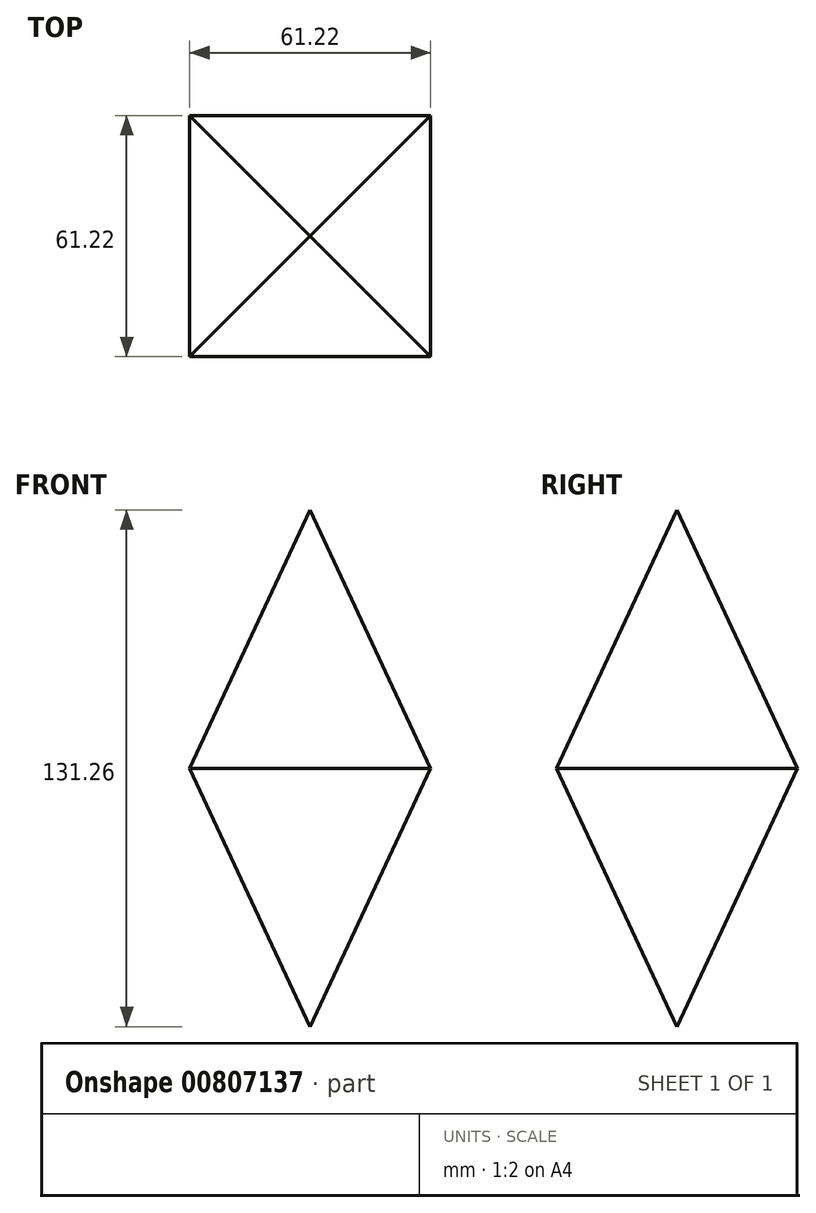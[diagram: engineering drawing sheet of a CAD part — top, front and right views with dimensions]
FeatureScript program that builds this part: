
annotation { "Feature Type Name" : "Feature", "Feature Type Description" : "" }
export const myFeature = defineFeature(function(context is Context, id is Id, definition is map)
    precondition{}
    {
        {
            var Q0;
            Q0=qCreatedBy(makeId("Top.planeOp"),FACE);
            var sketch = newSketch(context, id + "F0", { "sketchPlane" : qUnion([Q0])});
            skLineSegment(sketch, "E0.bottom", {"start": v(30.6, -30.6) * mm, "end": v(-30.6, -30.6) * mm});
            skLineSegment(sketch, "E0.top", {"start": v(30.6, 30.6) * mm, "end": v(-30.6, 30.6) * mm});
            skLineSegment(sketch, "E0.left", {"start": v(30.6, -30.6) * mm, "end": v(30.6, 30.6) * mm});
            skLineSegment(sketch, "E0.right", {"start": v(-30.6, -30.6) * mm, "end": v(-30.6, 30.6) * mm});
            skPoint(sketch, "E0.middle", {"position": v(0, 0) * mm});
            skSolve(sketch);
        }
        {
            var Q0;
            Q0=makeQuery(id+"F0.imprint","IMPRINT",FACE,{"disambiguationData":[TD([[makeQuery(id+"F0.imprint","IMPRINT",EDGE,{"derivedFrom":sQuery(id+"F0.wireOp",EDGE,"E0.bottom")}),-1.0]])]});
            extrude(context, id + "F1", {"entities" : qUnion([Q0]), "oppositeDirection" : true, "depth" : 67.06 * mm, "offsetDistance" : 25.4 * mm, "hasDraft" : true, "draftAngle" : 25 * degree, "draftPullDirection" : true, "hasSecondDirection" : true, "secondDirectionOppositeDirection" : false, "secondDirectionDepth" : 82.8 * mm, "hasSecondDirectionDraft" : true, "secondDirectionDraftAngle" : 25 * degree, "secondDirectionDraftPullDirection" : true});
        }
    });
